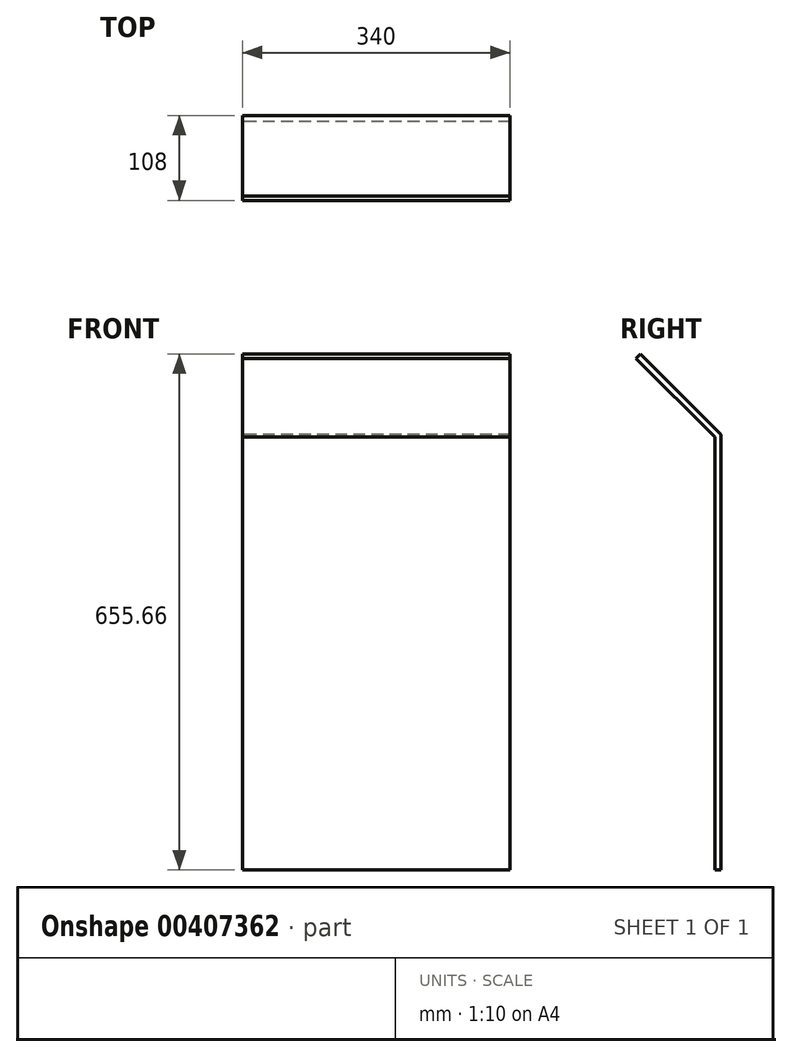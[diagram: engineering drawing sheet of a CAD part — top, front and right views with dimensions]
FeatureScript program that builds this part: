
annotation { "Feature Type Name" : "Feature", "Feature Type Description" : "" }
export const myFeature = defineFeature(function(context is Context, id is Id, definition is map)
    precondition{}
    {
        {
            var Q0;
            Q0=qCreatedBy(makeId("Right.planeOp"),FACE);
            var sketch = newSketch(context, id + "F0", { "sketchPlane" : qUnion([Q0])});
            skLineSegment(sketch, "E0", {"start": v(0, 0) * mm, "end": v(0, 550) * mm});
            skLineSegment(sketch, "E1", {"start": v(0, 550) * mm, "end": v(-100, 650) * mm});
            skLineSegment(sketch, "E2.0", {"start": v(8, 553.31) * mm, "end": v(-94.34, 655.66) * mm});
            skLineSegment(sketch, "E2.1", {"start": v(8, 0) * mm, "end": v(8, 553.31) * mm});
            skLineSegment(sketch, "E3", {"start": v(-94.34, 655.66) * mm, "end": v(-100, 650) * mm});
            skLineSegment(sketch, "E4", {"start": v(0, 0) * mm, "end": v(8, 0) * mm});
            skSolve(sketch);
        }
        {
            var Q0;
            Q0=makeQuery(id+"F0.imprint","IMPRINT",FACE,{"disambiguationData":[TD([[makeQuery(id+"F0.imprint","IMPRINT",EDGE,{"derivedFrom":sQuery(id+"F0.wireOp",EDGE,"E0")}),-1.0]])]});
            extrude(context, id + "F1", {"entities" : qUnion([Q0]), "depth" : 340 * mm});
        }
    });
